# Revit family: Haworth_ActiveComponents_RectangularHalfConferenceEnd_Intuity_BUILD
name_source: partatom
category: Furniture Systems
revit_build: Autodesk Revit Architecture 2015 (Build: 20141119_1515(x64)
units: mm (PartAtom-declared; Revit-internal decimal feet)

## types (4) — shared parameters
Accent Plate Finish = Haworth _ Paint _ Metallic Silver
Access Hatch Finish = Haworth _ Paint _ Metallic Silver
Access Hatch No = No
Access Hatch Yes = Yes
Access Plate Depth = 4 1/4"
Access Plate Height = 3/8"
Access Plate Offset = 7/8"
Actual Height = 29 3/16"
Actual Worksurface Depth = 19 1/2"
Assembly Code = E2020200
Beam Depth = 1 1/4"
Beam Gap = 9/16"
Beam Height = 2"
Beam Offset = 16 1/2"
Custom Screen Size = No
Custom Size = No
End Cap Depth Half = 5 29/32"
End Cap Offset = 1/8"
Leg Finish = Haworth _ Paint _ Metallic Silver
Leg Half = 1"
Leg Height = 28"
Manufacturer = Haworth
Max Depth = 30"
Max Screen Width = 72"
Max Width = 72"
Middle Void Dimension = 5 13/16"
Min Depth = 24"
Min Screen Width = 60"
Min Width = 60"
Model = WBYB
Overhang 18in = No
Overhang 9in = Yes
Overhang Dimension = 9"
Rail Finish = Haworth _ Paint _ Metallic Silver
Revision Number = 3
Screen Finish = Haworth _ Fabric _ Tellure _ Geranium 3A-42
Screen Offset = 28 1/4"
Size = Verify Final Dim. w/ Haworth
Standard Screen Widths = 60, 72 inches
Standard Worksurface Depths = 24, 30 inches
Standard Worksurface Widths = 60, 72 inches
Sustainability Info = http://www.haworth.com
Top Thickness = 1 3/16"
URL = www.haworth.com
URL - Product = https://www.haworth.com
Utility Tray Yes = Yes
Warranty = http://www.haworth.com

## per-type parameters (varying)
| type | 24 Depth | 30 Depth | Actual Depth | Actual Screen Width | Actual Width | Depth | Description | Screen Width | Total Depth | Width |
| 24d 72w | Yes | No | 25 1/2" | 71 3/4" | 81" | 19 11/16" | Haworth Intuity - Worksurface - Rectangular Half Conference End - 24d 72w | 72" | 51" | 72" |
| 24d 60w | Yes | No | 25 1/2" | 59 3/4" | 69" | 19 11/16" | Haworth Intuity - Worksurface - Rectangular Half Conference End - 24d 60w | 60" | 51" | 60" |
| 30d 60w | No | Yes | 31 1/2" | 59 3/4" | 69" | 25 11/16" | Haworth Intuity - Worksurface - Rectangular Half Conference End - 30d 60w | 60" | 63" | 60" |
| 30d 72w | No | Yes | 31 1/2" | 71 3/4" | 81" | 25 11/16" | Haworth Intuity - Worksurface - Rectangular Half Conference End - 30d 72w | 72" | 63" | 72" |

## geometry (parser evidence)
native form markers: Sweep x24
no freeform markers — native parametric forms only
